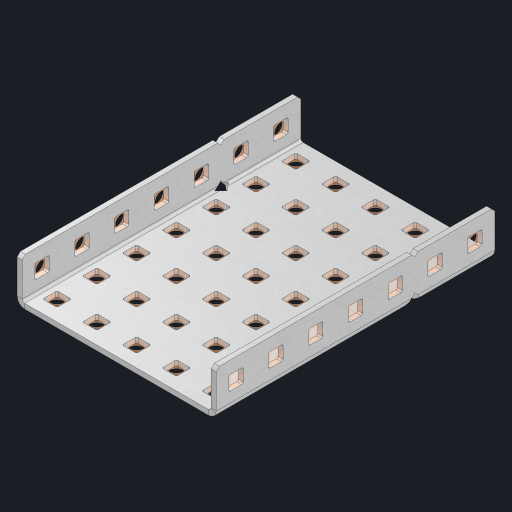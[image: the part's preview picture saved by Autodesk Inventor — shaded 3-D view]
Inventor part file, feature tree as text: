
AUTODESK INVENTOR PART (.ipt)
format: ipt  version: 2023 (Build 270158000, 158)  size: 833,024 bytes
history: native  units: in
note: dims shown in document units (in); Inventor stores cm internally (conversion verified against a paired STEP export)
features: other x54, extrude x48, sheet_metal_op x10, sketch x8, mirror x1, pattern_linear x1, chamfer x1
ambient origin geometry x8: Origin, YZ Plane, XZ Plane, XY Plane, X Axis, Y Axis, Z Axis, Center Point
bodies: Solid1 (feature_tree), Body (feature_tree)
feature tree (123):
  other  "Flange Pattern Plane"
  sheet_metal_op  "Flange Pattern"
  sheet_metal_op  "Body Pattern"
  other  "Arc Length"
  mirror  "Notch Mirror"
  pattern_linear  "Notch Pattern"  Spacing1=0.25in  [1 undecoded]
  chamfer  "End Chamfer"
  extrude  "Half Cut"  Depth=0.0625in
  sketch  "Sketch1"  dims[d0=2.5in]
  other  "Plate1"
  sketch  "Sketch2"  dims[d1=3.5in]
  other  "Plate2"
  sheet_metal_op  "Bend1"
  sheet_metal_op  "Corner1"
  sketch  "Sketch3"  dims[d2=0.0625in]
  other  "Flange Pattern Sketch"
  sketch  "Sketch7"  dims[d3=0.0625in]
  other  "Srf1"
  other  "Srf2"
  sketch  "Sketch8"  dims[d4=0.0312in]
  sketch  "Sketch9"  dims[d5=0.125in]
  other  "Srf91"
  sheet_metal_op  "Body Pattern Sketch"
  other  "Srf92"
  sketch  "Sketch13"  dims[d6=0.0625in]
  sketch  "Sketch14"  dims[d7=0.5in d8=90.0deg d9=0.0312in d10=0.25in d11=0.0625in d12=0.0625in d16=0.182in d17=0.02in d18=0.0625in d19=0.0in d20=0.25in d21=0.25in d46=0.172in d47=1.0in d48=0.0in d49=0.182in d50=0.02in d51=0.25in d52=0.25in d53=0.0625in d54=0.0in d55=0.172in d56=1.0in d57=0.0in d60=2.7559in d62=0.5in d63=1.9685in d65=0.5in d85=0.1473in d86=0.1782in d88=0.04in d89=0.0625in d90=0.0in d91=0.04in d92=0.0491in d95=2.5in d96=0.04in d97=0.25in d98=45.0deg d101=0.0in d102=2.497in d131=2.5in d132=2.7559in d134=0.5in d139=0.5in]
  other  "Srf856"
  other  "Srf1310"
  other  "Srf1311"
  other  "Srf1312"
  other  "Srf1376"
  other  "Srf1377"
  other  "Srf1728"
  other  "Srf1755"
  other  "Srf1878"
  other  "Srf1879"
  other  "Srf1880"
  other  "Srf1881"
  other  "Srf1882"
  other  "Srf1883"
  other  "Srf1884"
  other  "Srf1885"
  other  "Srf1942"
  other  "Srf1943"
  other  "Srf1944"
  other  "Srf1945"
  other  "Srf1946"
  other  "Srf1947"
  other  "Srf1948"
  other  "Srf1949"
  other  "Srf1950"
  other  "Srf1951"
  other  "Srf1952"
  other  "Srf1953"
  other  "Srf1954"
  other  "Srf1955"
  other  "Srf1956"
  other  "Srf1957"
  other  "Srf1958"
  other  "Srf1959"
  other  "Srf1960"
  other  "Srf1961"
  other  "Srf1962"
  other  "Srf1963"
  other  "Srf1964"
  other  "Srf1965"
  other  "Srf1966"
  other  "Srf1967"
  other  "Srf1968"
  other  "Srf1969"
  other  "Srf1970"
  sheet_metal_op  "Flange Stamp"
  sheet_metal_op  "Flange Circle"
  sheet_metal_op  "Body Stamp"
  sheet_metal_op  "Body Circle"
  sheet_metal_op  "Notch"
  extrude  "ExtrusionSrf2"  Depth=0.0625in
  extrude  "ExtrusionSrf92"  Depth=2.5in
  extrude  "ExtrusionSrf856"  Depth=0.02in
  extrude  "ExtrusionSrf1310"  Depth=0.0625in
  extrude  "ExtrusionSrf1311"  TaperAngle=0.0deg  [1 undecoded]
  extrude  "ExtrusionSrf1312"  Depth=0.25in
  extrude  "ExtrusionSrf1376"  Depth=0.25in
  extrude  "ExtrusionSrf1377"  Depth=2.5in
  extrude  "ExtrusionSrf1728"  Depth=2.5in TaperAngle=0.0deg
  extrude  "ExtrusionSrf1755"  Depth=2.5in
  extrude  "ExtrusionSrf1878"  Depth=0.02in
  extrude  "ExtrusionSrf1879"  Depth=0.25in
  extrude  "ExtrusionSrf1880"  Depth=0.25in
  extrude  "ExtrusionSrf1881"  Depth=0.0625in
  extrude  "ExtrusionSrf1882"  TaperAngle=0.0deg  [1 undecoded]
  extrude  "ExtrusionSrf1883"  Depth=2.5in
  extrude  "ExtrusionSrf1884"  Depth=2.5in TaperAngle=0.0deg
  extrude  "ExtrusionSrf1885"  Depth=2.5in
  extrude  "ExtrusionSrf1942"  Depth=2.5in
  extrude  "ExtrusionSrf1943"  Depth=2.5in
  extrude  "ExtrusionSrf1944"  Depth=2.5in
  extrude  "ExtrusionSrf1945"  Depth=2.5in
  extrude  "ExtrusionSrf1946"  Depth=0.0625in
  extrude  "ExtrusionSrf1947"  TaperAngle=0.0deg  [1 undecoded]
  extrude  "ExtrusionSrf1948"  Depth=2.5in
  extrude  "ExtrusionSrf1949"  Depth=2.5in
  extrude  "ExtrusionSrf1950"  Depth=2.5in
  extrude  "ExtrusionSrf1951"  Depth=0.25in TaperAngle=45.0deg
  extrude  "ExtrusionSrf1952"  TaperAngle=0.0deg  [1 undecoded]
  extrude  "ExtrusionSrf1953"  Depth=2.5in
  extrude  "ExtrusionSrf1954"  Depth=2.5in
  extrude  "ExtrusionSrf1955"  Depth=2.5in
  extrude  "ExtrusionSrf1956"  Depth=2.5in
  extrude  "ExtrusionSrf1957"  Depth=2.5in
  extrude  "ExtrusionSrf1958"  [1 undecoded]
  extrude  "ExtrusionSrf1959"  [1 undecoded]
  extrude  "ExtrusionSrf1960"  [1 undecoded]
  extrude  "ExtrusionSrf1961"  [1 undecoded]
  extrude  "ExtrusionSrf1962"  [1 undecoded]
  extrude  "ExtrusionSrf1963"  [1 undecoded]
  extrude  "ExtrusionSrf1964"  [1 undecoded]
  extrude  "ExtrusionSrf1965"  [1 undecoded]
  extrude  "ExtrusionSrf1966"  [1 undecoded]
  extrude  "ExtrusionSrf1967"  [1 undecoded]
  extrude  "ExtrusionSrf1968"  [1 undecoded]
  extrude  "ExtrusionSrf1969"  [1 undecoded]
  extrude  "ExtrusionSrf1970"  [1 undecoded]
note: 18 required parameter values undecoded (feature->parameter linkage not recoverable at this tier; creation-order binding heuristic only, values carry confidence <= 0.55)
